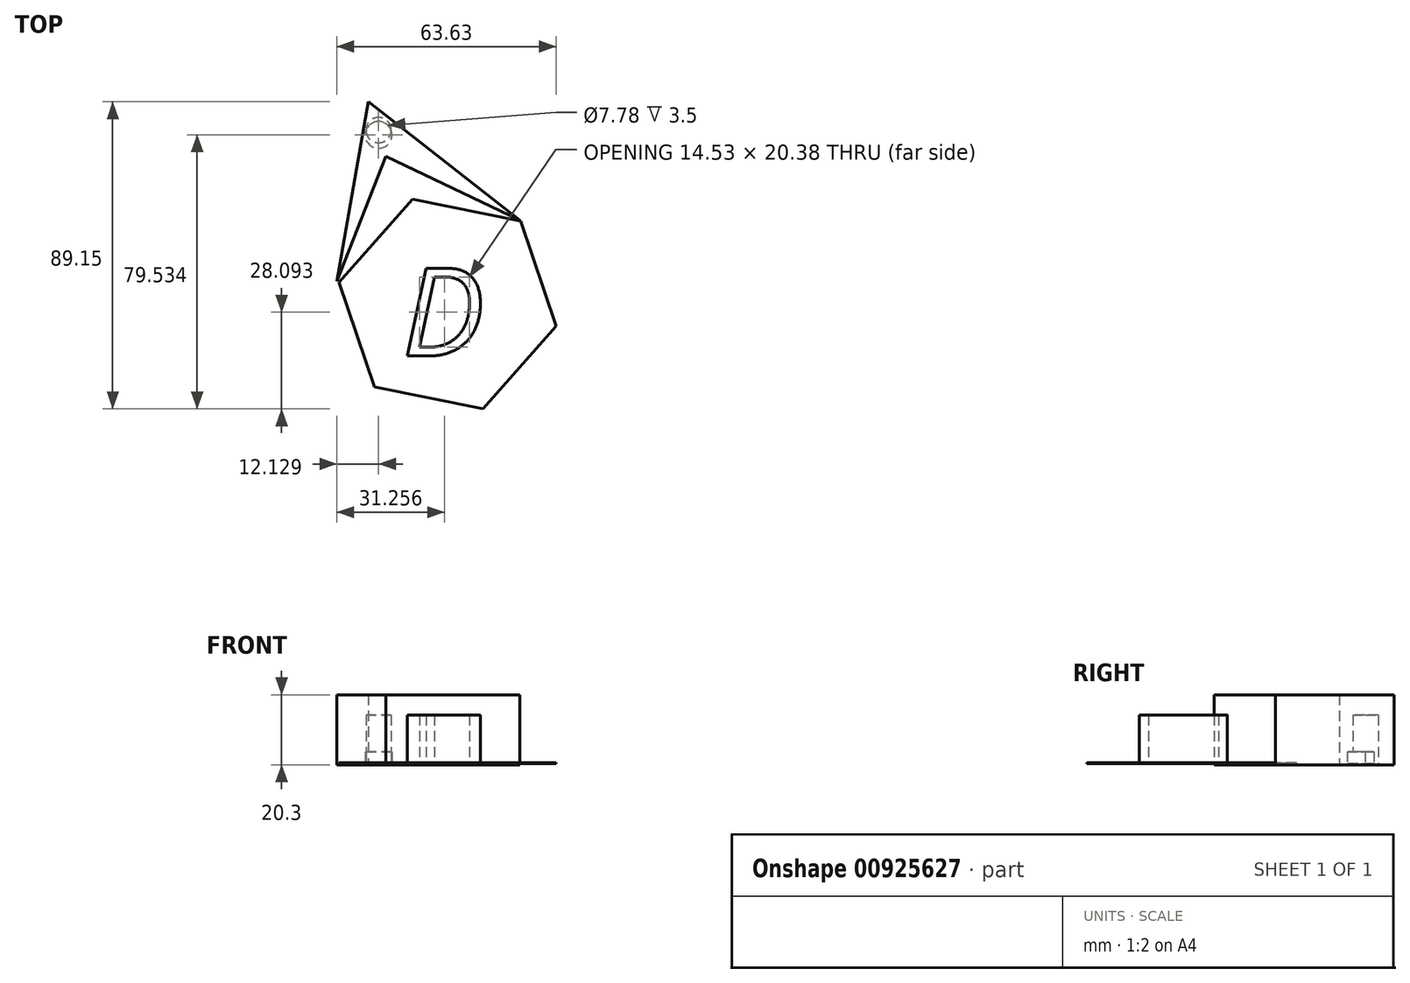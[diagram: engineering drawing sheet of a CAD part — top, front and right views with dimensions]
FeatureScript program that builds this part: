
annotation { "Feature Type Name" : "Feature", "Feature Type Description" : "" }
export const myFeature = defineFeature(function(context is Context, id is Id, definition is map)
    precondition{}
    {
        {
            var Q0;
            Q0=qCreatedBy(makeId("Top.planeOp"),FACE);
            var sketch = newSketch(context, id + "F0", { "sketchPlane" : qUnion([Q0])});
            skCircle(sketch, "E0", {"center": v(0, 0) * mm, "radius": 35.48 * mm});
            skCircle(sketch, "E1.cCircle", {"center": v(0, 0) * mm, "radius": 27.8 * mm, "construction": true});
            skLineSegment(sketch, "E1.0", {"start": v(-21.23, -24.08) * mm, "end": v(-31.47, 6.35) * mm});
            skLineSegment(sketch, "E1.1", {"start": v(-31.47, 6.35) * mm, "end": v(-10.23, 30.43) * mm});
            skLineSegment(sketch, "E1.2", {"start": v(-10.23, 30.43) * mm, "end": v(21.23, 24.08) * mm});
            skLineSegment(sketch, "E1.3", {"start": v(21.23, 24.08) * mm, "end": v(31.47, -6.35) * mm});
            skLineSegment(sketch, "E1.4", {"start": v(31.47, -6.35) * mm, "end": v(10.23, -30.43) * mm});
            skLineSegment(sketch, "E1.5", {"start": v(10.23, -30.43) * mm, "end": v(-21.23, -24.08) * mm});
            skPoint(sketch, "E1.0.midPoint", {"position": v(-26.35, -8.86) * mm});
            skSolve(sketch);
        }
        {
            var Q0;
            Q0=makeQuery(id+"F0.imprint","IMPRINT",FACE,{"disambiguationData":[TD([[makeQuery(id+"F0.imprint","IMPRINT",EDGE,{"derivedFrom":sQuery(id+"F0.wireOp",EDGE,"E1.0")}),-1.0]])]});
            extrude(context, id + "F1", {"entities" : qUnion([Q0]), "depth" : 0.3 * mm, "offsetDistance" : 25 * mm});
        }
        {
            var Q0;
            Q0=qCreatedBy(makeId("Top.planeOp"),FACE);
            var sketch = newSketch(context, id + "F2", { "sketchPlane" : qUnion([Q0])});
            skLineSegment(sketch, "E2", {"start": v(-32.16, 6.52) * mm, "end": v(-23, 58.72) * mm});
            skLineSegment(sketch, "E3", {"start": v(20.95, 24.38) * mm, "end": v(-23, 58.72) * mm});
            skLineSegment(sketch, "E4", {"start": v(-32.16, 6.52) * mm, "end": v(-17.97, 42.92) * mm});
            skLineSegment(sketch, "E5", {"start": v(-17.97, 42.92) * mm, "end": v(20.95, 24.38) * mm});
            skSolve(sketch);
        }
        {
            var Q0;
            Q0 = qSketchRegion(id + "F2", true);
            extrude(context, id + "F3", {"entities" : qUnion([Q0]), "depth" : 20 * mm, "offsetDistance" : 25 * mm});
        }
        {
            var Q0;
            Q0=makeQuery(id+"F3.opExtrude","CAP_FACE",FACE,{"disambiguationData":[OSD([sQuery(id+"F2.wireOp",EDGE,"E2"),sQuery(id+"F2.wireOp",EDGE,"E3"),sQuery(id+"F2.wireOp",EDGE,"E4"),sQuery(id+"F2.wireOp",EDGE,"E5")])],"isStart":false});
            extrude(context, id + "F4", {"entities" : qUnion([Q0]), "operationType" : NewBodyOperationType.ADD, "oppositeDirection" : true, "depth" : 13.9 * mm, "offsetDistance" : 25 * mm});
        }
        {
            var Q0;
            Q0=makeQuery(id+"F3.opExtrude","CAP_FACE",FACE,{"disambiguationData":[OSD([sQuery(id+"F2.wireOp",EDGE,"E2"),sQuery(id+"F2.wireOp",EDGE,"E3"),sQuery(id+"F2.wireOp",EDGE,"E4"),sQuery(id+"F2.wireOp",EDGE,"E5")])],"isStart":false});
            extrude(context, id + "F5", {"entities" : qUnion([Q0]), "operationType" : NewBodyOperationType.ADD, "oppositeDirection" : true, "depth" : 20.3 * mm, "offsetDistance" : 25 * mm});
        }
        {
            var Q0;
            Q0=makeQuery(id+"F3.opExtrude","CAP_FACE",FACE,{"disambiguationData":[OSD([sQuery(id+"F2.wireOp",EDGE,"E2"),sQuery(id+"F2.wireOp",EDGE,"E3"),sQuery(id+"F2.wireOp",EDGE,"E4"),sQuery(id+"F2.wireOp",EDGE,"E5")])],"isStart":false});
            extrude(context, id + "F6", {"entities" : qUnion([Q0]), "operationType" : NewBodyOperationType.ADD, "oppositeDirection" : true, "depth" : 16.6 * mm, "offsetDistance" : 25 * mm});
        }
        {
            var Q0;
            Q0=makeQuery(id+"F3.opExtrude","CAP_FACE",FACE,{"disambiguationData":[OSD([sQuery(id+"F2.wireOp",EDGE,"E2"),sQuery(id+"F2.wireOp",EDGE,"E3"),sQuery(id+"F2.wireOp",EDGE,"E4"),sQuery(id+"F2.wireOp",EDGE,"E5")])],"isStart":false});
            extrude(context, id + "F7", {"entities" : qUnion([Q0]), "operationType" : NewBodyOperationType.ADD, "oppositeDirection" : true, "depth" : 6.6 * mm, "offsetDistance" : 25 * mm});
        }
        {
            var Q0;
            Q0=qCreatedBy(makeId("Top.planeOp"),FACE);
            var sketch = newSketch(context, id + "F8", { "sketchPlane" : qUnion([Q0])});
            skText(sketch, "E6", { "text": "D", "fontName": "OpenSans-Italic.ttf"});
            skCircle(sketch, "E7", {"center": v(-20.03, 50.48) * mm, "radius": 3.67 * mm});
            const initialGuessF8  = {"E6": [-0.01318, -0.01509, 1, 0, 0.02573]};
            skSetInitialGuess(sketch, initialGuessF8);
            skSolve(sketch);
        }
        {
            var Q0;
            Q0 = qSketchRegion(id + "F8", true);
            var Q1;
            Q1=sQuery(id+"F8.wireOp",EDGE,"E7");
            extrude(context, id + "F9", {"entities" : qUnion([Q0]), "surfaceEntities" : qUnion([Q1]), "depth" : 14.1 * mm, "offsetDistance" : 25 * mm});
        }
        {
            var Q0;
            Q0=qCreatedBy(makeId("Top.planeOp"),FACE);
            var sketch = newSketch(context, id + "F10", { "sketchPlane" : qUnion([Q0])});
            skCircle(sketch, "E8", {"center": v(-20.03, 49.1) * mm, "radius": 3.9 * mm});
            skSolve(sketch);
        }
        {
            var Q0;
            Q0 = qSketchRegion(id + "F10", true);
            extrude(context, id + "F11", {"entities" : qUnion([Q0]), "operationType" : NewBodyOperationType.REMOVE, "depth" : 3.5 * mm, "offsetDistance" : 25 * mm});
        }
    });
